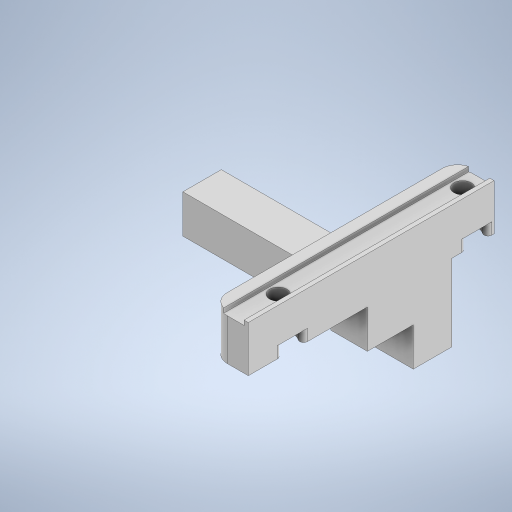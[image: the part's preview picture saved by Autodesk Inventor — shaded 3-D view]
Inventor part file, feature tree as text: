
AUTODESK INVENTOR PART (.ipt)
format: ipt  version: 2024 (Build 280153000, 153)  size: 317,440 bytes
history: native  units: in
note: dims shown in document units (in); Inventor stores cm internally (conversion verified against a paired STEP export)
features: extrude x5, sketch x5, projected_geometry x4, fillet x2
ambient origin geometry x8: Origin, YZ Plane, XZ Plane, XY Plane, X Axis, Y Axis, Z Axis, Center Point
bodies: Solid1 (feature_tree)
feature tree (16):
  extrude  "Extrusion1"  Depth=2.5197in
  extrude  "Extrusion2"  Depth=1.8898in
  extrude  "Extrusion3"  Depth=0.4724in TaperAngle=0.0deg
  fillet  "Fillet1"  Radius=0.0433in
  fillet  "Fillet2"  Radius=0.2126in
  extrude  "Extrusion17"  Depth=0.4724in TaperAngle=0.0deg
  extrude  "Extrusion18"  Depth=0.1181in TaperAngle=0.0deg
  sketch  "Sketch1"  dims[d1=0.374in d2=2.5197in]
  sketch  "Sketch2"  dims[d3=0.1772in d4=1.8898in]
  sketch  "Sketch3"  dims[d6=0.1457in d7=0.4724in d8=0.0in d9=0.0433in d10=0.2126in]
  projected_geometry  "Projected Loop2"
  projected_geometry  "Projected Loop3"
  projected_geometry  "Projected Loop4"
  projected_geometry  "Projected Loop5"
  sketch  "Sketch17"  dims[d11=0.0472in d12=0.4724in d13=0.0in]
  sketch  "Sketch18"  dims[d14=0.2953in d15=0.1181in d16=0.0in d17=0.1772in d18=0.0394in d19=0.1575in d76=0.4724in d90=0.102in d91=0.8661in d92=0.3937in d93=0.0in d94=2.3622in d95=0.3937in d96=0.3937in d97=0.0in d42=0.0197in d43=0.0344in d44=0.0197in d45=0.0344in d46=0.0in d47=0.0in d48=0.0in d49=0.0in d50=0.0in d51=0.0in d52=0.0in d53=0.0in d55=0.0197in d56=0.0344in d57=0.0197in d58=0.0344in d60=0.0197in d61=0.0344in d62=0.0197in d63=0.0344in d72=0.0197in d73=0.0344in d74=0.0197in d75=0.0344in]
